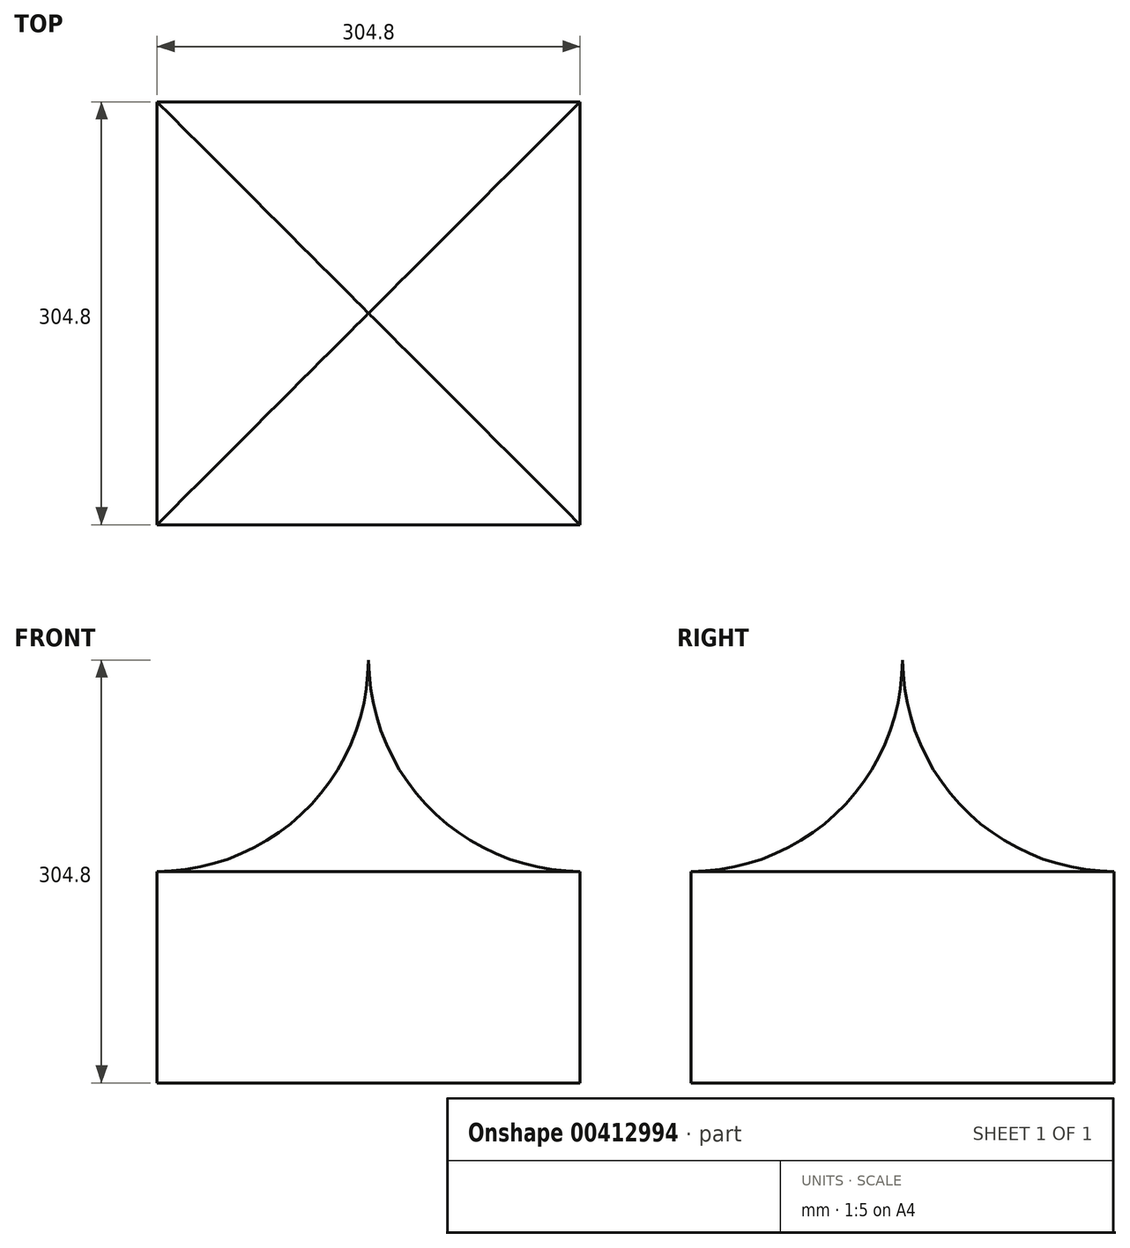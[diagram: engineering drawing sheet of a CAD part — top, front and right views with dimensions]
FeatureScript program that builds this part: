
annotation { "Feature Type Name" : "Feature", "Feature Type Description" : "" }
export const myFeature = defineFeature(function(context is Context, id is Id, definition is map)
    precondition{}
    {
        {
            var Q0;
            Q0=qCreatedBy(makeId("Top.planeOp"),FACE);
            var sketch = newSketch(context, id + "F0", { "sketchPlane" : qUnion([Q0])});
            skLineSegment(sketch, "E0.bottom", {"start": v(152.4, -152.4) * mm, "end": v(-152.4, -152.4) * mm});
            skLineSegment(sketch, "E0.top", {"start": v(152.4, 152.4) * mm, "end": v(-152.4, 152.4) * mm});
            skLineSegment(sketch, "E0.left", {"start": v(152.4, -152.4) * mm, "end": v(152.4, 152.4) * mm});
            skLineSegment(sketch, "E0.right", {"start": v(-152.4, -152.4) * mm, "end": v(-152.4, 152.4) * mm});
            skPoint(sketch, "E0.middle", {"position": v(0, 0) * mm});
            skSolve(sketch);
        }
        {
            var Q0;
            Q0=makeQuery(id+"F0.imprint","IMPRINT",FACE,{"disambiguationData":[TD([[makeQuery(id+"F0.imprint","IMPRINT",EDGE,{"derivedFrom":sQuery(id+"F0.wireOp",EDGE,"E0.bottom")}),-1.0]])]});
            extrude(context, id + "F1", {"entities" : qUnion([Q0]), "endBound" : BoundingType.SYMMETRIC, "oppositeDirection" : true, "depth" : 304.8 * mm});
        }
        {
            var Q0;
            Q0=qCreatedBy(makeId("Right.planeOp"),FACE);
            var sketch = newSketch(context, id + "F2", { "sketchPlane" : qUnion([Q0])});
            skCircle(sketch, "E1", {"center": v(-152.4, 152.4) * mm, "radius": 152.4 * mm});
            skLineSegment(sketch, "E2.bottom", {"start": v(0, 0) * mm, "end": v(-152.4, 0) * mm});
            skLineSegment(sketch, "E2.top", {"start": v(0, 152.4) * mm, "end": v(-152.4, 152.4) * mm});
            skLineSegment(sketch, "E2.left", {"start": v(0, 0) * mm, "end": v(0, 152.4) * mm});
            skLineSegment(sketch, "E2.right", {"start": v(-152.4, 0) * mm, "end": v(-152.4, 152.4) * mm});
            skLineSegment(sketch, "E3.bottom", {"start": v(0, 0) * mm, "end": v(152.4, 0) * mm});
            skLineSegment(sketch, "E3.top", {"start": v(0, 152.4) * mm, "end": v(152.4, 152.4) * mm});
            skLineSegment(sketch, "E3.right", {"start": v(152.4, 0) * mm, "end": v(152.4, 152.4) * mm});
            skCircle(sketch, "E4", {"center": v(152.4, 152.4) * mm, "radius": 152.4 * mm});
            skSolve(sketch);
        }
        {
            var Q0;
            {var subQ2=sQuery(id+"F2.wireOp",EDGE,"E2.top");Q0=makeQuery(id+"F2.imprint","IMPRINT",FACE,{"disambiguationData":[TD([[makeQuery(id+"F2.imprint","IMPRINT",EDGE,{"derivedFrom":subQ2}),-1.0]])]});}
            var Q1;
            {var subQ2=sQuery(id+"F2.wireOp",EDGE,"E2.top");Q1=makeQuery(id+"F2.imprint","IMPRINT",FACE,{"disambiguationData":[TD([[makeQuery(id+"F2.imprint","IMPRINT",EDGE,{"derivedFrom":subQ2}),1.0]])]});}
            var Q2;
            {var subQ0=sQuery(id+"F2.wireOp",EDGE,"E3.top");Q2=makeQuery(id+"F2.imprint","IMPRINT",FACE,{"disambiguationData":[TD([[makeQuery(id+"F2.imprint","IMPRINT",EDGE,{"derivedFrom":subQ0}),-1.0]])]});}
            extrude(context, id + "F3", {"entities" : qUnion([Q0, Q1, Q2]), "operationType" : NewBodyOperationType.REMOVE, "endBound" : BoundingType.SYMMETRIC, "oppositeDirection" : true, "depth" : 304.8 * mm});
        }
        {
            var Q0;
            Q0=qCreatedBy(makeId("Front.planeOp"),FACE);
            var sketch = newSketch(context, id + "F4", { "sketchPlane" : qUnion([Q0])});
            skCircle(sketch, "E5", {"center": v(-152.4, 152.4) * mm, "radius": 152.4 * mm});
            skLineSegment(sketch, "E6.bottom", {"start": v(0, 0) * mm, "end": v(-152.4, 0) * mm});
            skLineSegment(sketch, "E6.top", {"start": v(0, 152.4) * mm, "end": v(-152.4, 152.4) * mm});
            skLineSegment(sketch, "E6.left", {"start": v(0, 0) * mm, "end": v(0, 152.4) * mm});
            skLineSegment(sketch, "E6.right", {"start": v(-152.4, 0) * mm, "end": v(-152.4, 152.4) * mm});
            skLineSegment(sketch, "E7.bottom", {"start": v(0, 0) * mm, "end": v(152.4, 0) * mm});
            skLineSegment(sketch, "E7.top", {"start": v(0, 152.4) * mm, "end": v(152.4, 152.4) * mm});
            skLineSegment(sketch, "E7.right", {"start": v(152.4, 0) * mm, "end": v(152.4, 152.4) * mm});
            skCircle(sketch, "E8", {"center": v(152.4, 152.4) * mm, "radius": 152.4 * mm});
            skSolve(sketch);
        }
        {
            var Q0;
            {var subQ0=sQuery(id+"F4.wireOp",EDGE,"E7.top");Q0=makeQuery(id+"F4.imprint","IMPRINT",FACE,{"disambiguationData":[TD([[makeQuery(id+"F4.imprint","IMPRINT",EDGE,{"derivedFrom":subQ0}),-1.0]])]});}
            var Q1;
            {var subQ2=sQuery(id+"F4.wireOp",EDGE,"E6.top");Q1=makeQuery(id+"F4.imprint","IMPRINT",FACE,{"disambiguationData":[TD([[makeQuery(id+"F4.imprint","IMPRINT",EDGE,{"derivedFrom":subQ2}),1.0]])]});}
            extrude(context, id + "F5", {"entities" : qUnion([Q0, Q1]), "operationType" : NewBodyOperationType.REMOVE, "endBound" : BoundingType.SYMMETRIC, "oppositeDirection" : true, "depth" : 304.8 * mm});
        }
    });
